# Revit family: Verano_V762_Talamanca_GM_R21
name_source: partatom
category: Generic Models
units: mm (PartAtom-declared; Revit-internal decimal feet)

## family parameters
Always vertical = Yes
Can host rebar = No
Cut with Voids When Loaded = No
Part Type = Normal
Room Calculation Point = No
Round Connector Dimension = Use Diameter
Shared = No
Work Plane-Based = No

## types (4) — shared parameters
Frame Material = V_Antracite
Manufacturer = Verano Systems
Maximal Height = 3000 mm  [stored 9.84252 ft]
Minimal Height = 1000 mm  [stored 3.28084 ft]
Model = V762 Talamanca
URL = https://verano.nl
zero-valued in all types: Default Elevation, Opening Minimum

## per-type parameters (varying)
| type | 3 Track | 3rd | 4 Track | 5 Track | 6 Track | Maximal Width | Minimal Width | TRACKS |
| 3 Track | Yes | No | No | No | No | 3250 mm  [stored 10.6627 ft] | 2000 mm  [stored 6.56168 ft] | 3 |
| 4 Track | No | Yes | Yes | No | No | 4500 mm | 3000 mm  [stored 9.84252 ft] | 4 |
| 5 Track | No | Yes | No | Yes | No | 5500 mm  [stored 18.0446 ft] | 4000 mm  [stored 13.1234 ft] | 5 |
| 6 Track | No | Yes | No | No | Yes | 6000 mm  [stored 19.685 ft] | 4500 mm | 6 |

note: [stored X ft] marks values corroborated as IEEE doubles in the binary element streams (Revit-internal decimal feet)

## geometry (parser evidence)
native form markers: Sweep x13
no freeform markers — native parametric forms only
